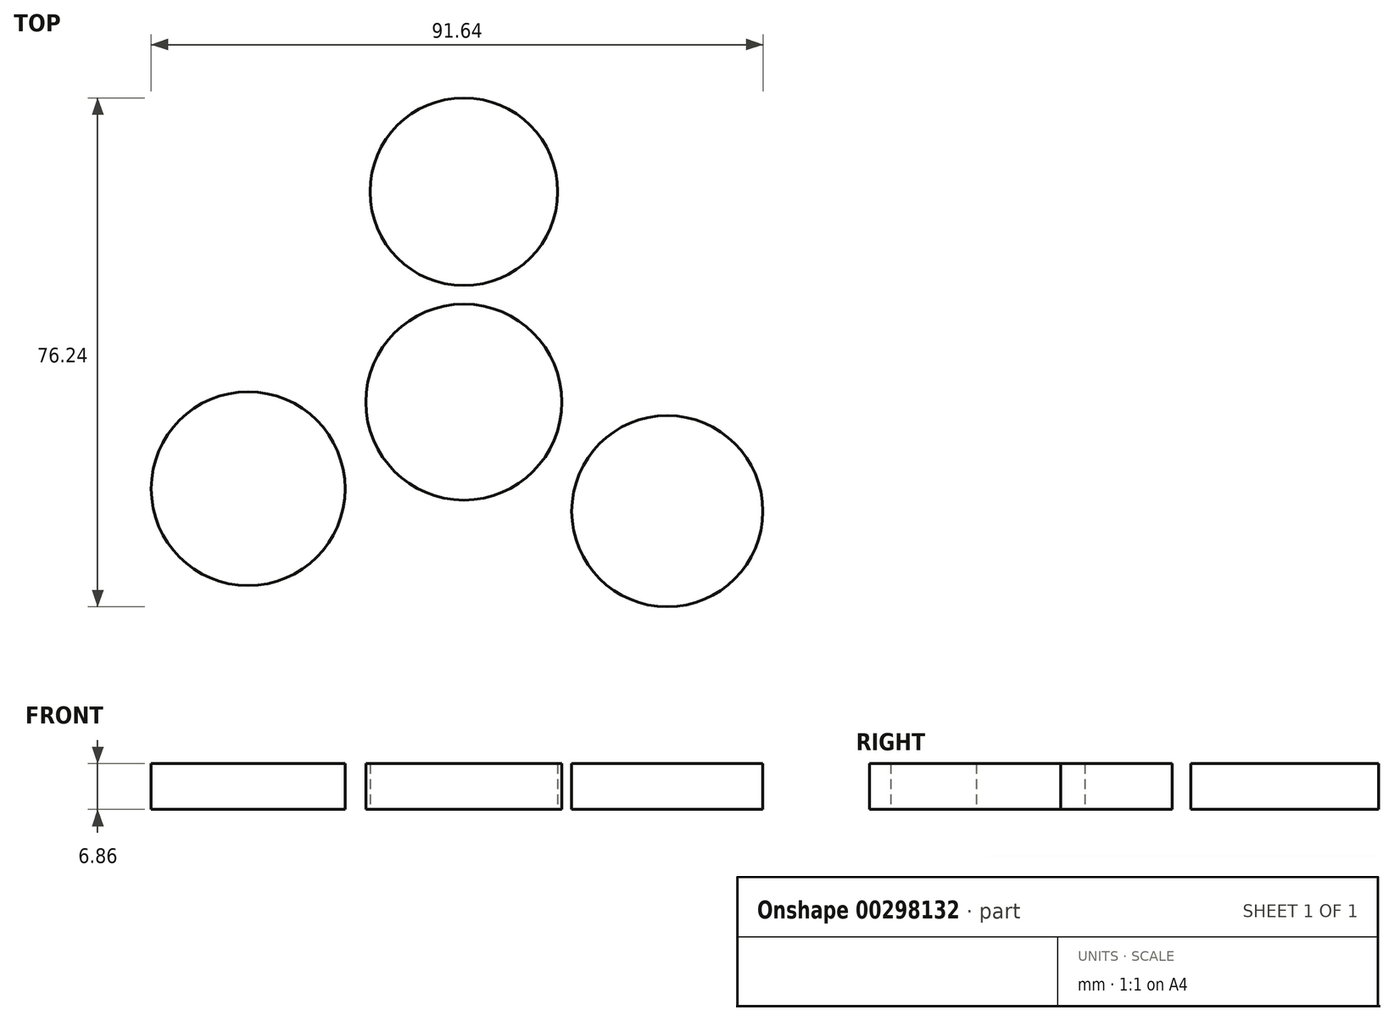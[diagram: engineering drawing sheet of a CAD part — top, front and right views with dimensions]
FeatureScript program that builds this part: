
annotation { "Feature Type Name" : "Feature", "Feature Type Description" : "" }
export const myFeature = defineFeature(function(context is Context, id is Id, definition is map)
    precondition{}
    {
        {
            var Q0;
            Q0=qCreatedBy(makeId("Top.planeOp"),FACE);
            var sketch = newSketch(context, id + "F0", { "sketchPlane" : qUnion([Q0])});
            skCircle(sketch, "E0", {"center": v(0, 0) * mm, "radius": 14.68 * mm});
            skCircle(sketch, "E1", {"center": v(0, 31.52) * mm, "radius": 14.06 * mm});
            skCircle(sketch, "E2", {"center": v(30.48, -16.34) * mm, "radius": 14.32 * mm});
            skCircle(sketch, "E3", {"center": v(-32.31, -12.97) * mm, "radius": 14.52 * mm});
            skSolve(sketch);
        }
        {
            var Q0;
            Q0=makeQuery(id+"F0.imprint","IMPRINT",FACE,{"disambiguationData":[TD([[makeQuery(id+"F0.imprint","IMPRINT",EDGE,{"derivedFrom":sQuery(id+"F0.wireOp",EDGE,"E2")}),1.0]])]});
            var Q1;
            Q1=makeQuery(id+"F0.imprint","IMPRINT",FACE,{"disambiguationData":[TD([[makeQuery(id+"F0.imprint","IMPRINT",EDGE,{"derivedFrom":sQuery(id+"F0.wireOp",EDGE,"E0")}),1.0]])]});
            var Q2;
            Q2=makeQuery(id+"F0.imprint","IMPRINT",FACE,{"disambiguationData":[TD([[makeQuery(id+"F0.imprint","IMPRINT",EDGE,{"derivedFrom":sQuery(id+"F0.wireOp",EDGE,"E1")}),1.0]])]});
            var Q3;
            Q3=makeQuery(id+"F0.imprint","IMPRINT",FACE,{"disambiguationData":[TD([[makeQuery(id+"F0.imprint","IMPRINT",EDGE,{"derivedFrom":sQuery(id+"F0.wireOp",EDGE,"E3")}),1.0]])]});
            extrude(context, id + "F1", {"entities" : qUnion([Q0, Q1, Q2, Q3]), "depth" : 6.86 * mm});
        }
    });
